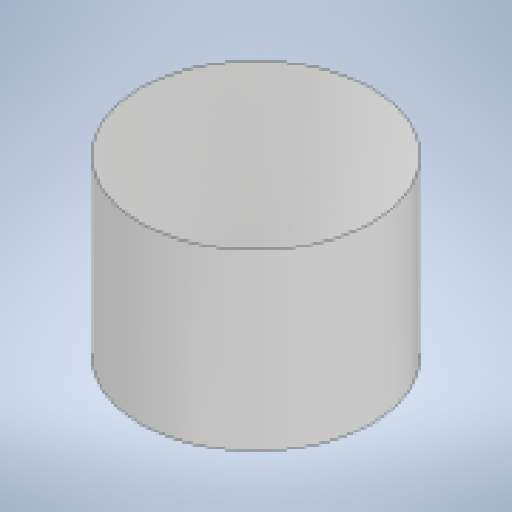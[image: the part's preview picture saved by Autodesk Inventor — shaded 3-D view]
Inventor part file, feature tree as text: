
AUTODESK INVENTOR PART (.ipt)
format: ipt  version: 2025.1 (Build 291241020, 241B)  size: 187,392 bytes
history: native  units: mm
features: extrude x1, sketch x1
ambient origin geometry x8: Origin, YZ Plane, XZ Plane, XY Plane, X Axis, Y Axis, Z Axis, Center Point
bodies: Solid1 (feature_tree)
feature tree (2):
  extrude  "Extrusion1"  Depth=15.0mm TaperAngle=0.0deg
  sketch  "Sketch1"  dims[d0=20.0mm d1=15.0mm d2=0.0mm]
